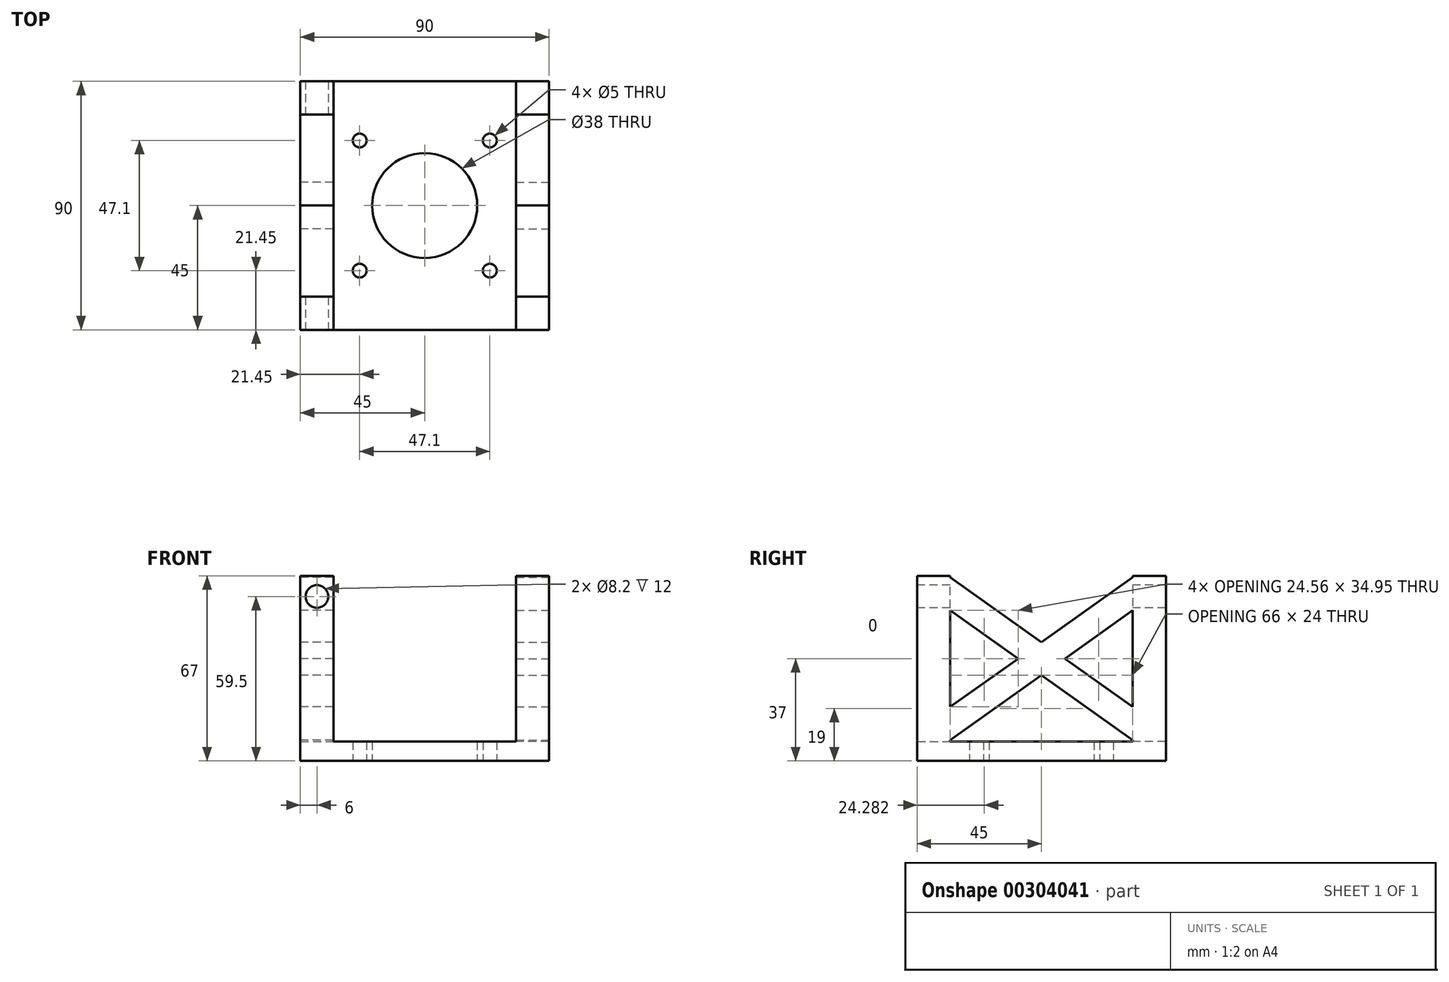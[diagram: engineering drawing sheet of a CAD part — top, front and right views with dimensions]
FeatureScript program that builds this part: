
annotation { "Feature Type Name" : "Feature", "Feature Type Description" : "" }
export const myFeature = defineFeature(function(context is Context, id is Id, definition is map)
    precondition{}
    {
        {
            var Q0;
            Q0=qCreatedBy(makeId("Top.planeOp"),FACE);
            var sketch = newSketch(context, id + "F0", { "sketchPlane" : qUnion([Q0])});
            skLineSegment(sketch, "E0.bottom", {"start": v(45, -45) * mm, "end": v(-45, -45) * mm});
            skLineSegment(sketch, "E0.top", {"start": v(45, 45) * mm, "end": v(-45, 45) * mm});
            skLineSegment(sketch, "E0.left", {"start": v(45, -45) * mm, "end": v(45, 45) * mm});
            skLineSegment(sketch, "E0.right", {"start": v(-45, -45) * mm, "end": v(-45, 45) * mm});
            skPoint(sketch, "E0.middle", {"position": v(0, 0) * mm});
            skLineSegment(sketch, "E1.bottom", {"start": v(23.55, -23.55) * mm, "end": v(-23.55, -23.55) * mm, "construction": true});
            skLineSegment(sketch, "E1.top", {"start": v(23.55, 23.55) * mm, "end": v(-23.55, 23.55) * mm, "construction": true});
            skLineSegment(sketch, "E1.left", {"start": v(23.55, -23.55) * mm, "end": v(23.55, 23.55) * mm, "construction": true});
            skLineSegment(sketch, "E1.right", {"start": v(-23.55, -23.55) * mm, "end": v(-23.55, 23.55) * mm, "construction": true});
            skCircle(sketch, "E2", {"center": v(0, 0) * mm, "radius": 19 * mm});
            skCircle(sketch, "E3", {"center": v(-23.55, 23.55) * mm, "radius": 2.5 * mm});
            skCircle(sketch, "E4", {"center": v(23.55, 23.55) * mm, "radius": 2.5 * mm});
            skCircle(sketch, "E5", {"center": v(23.55, -23.55) * mm, "radius": 2.5 * mm});
            skCircle(sketch, "E6", {"center": v(-23.55, -23.55) * mm, "radius": 2.5 * mm});
            skSolve(sketch);
        }
        {
            var Q0;
            Q0=makeQuery(id+"F0.imprint","IMPRINT",FACE,{"disambiguationData":[TD([[makeQuery(id+"F0.imprint","IMPRINT",EDGE,{"derivedFrom":sQuery(id+"F0.wireOp",EDGE,"E0.bottom")}),-1.0]])]});
            extrude(context, id + "F1", {"entities" : qUnion([Q0]), "depth" : 7 * mm});
        }
        {
            var Q0;
            Q0=makeQuery(id+"F1.opExtrude","CAP_FACE",FACE,{"disambiguationData":[OSD([sQuery(id+"F0.wireOp",EDGE,"E0.bottom"),sQuery(id+"F0.wireOp",EDGE,"E0.top"),sQuery(id+"F0.wireOp",EDGE,"E0.left"),sQuery(id+"F0.wireOp",EDGE,"E0.right")])],"isStart":false});
            cPlane(context, id + "F2", {"entities" : qUnion([Q0]), "cplaneType" : CPlaneType.OFFSET, "offset" : 0 * mm, "width" : 150 * mm, "height" : 150 * mm});
        }
        {
            var Q0;
            Q0=qCreatedBy(id+"F2.planeOp",FACE);
            var sketch = newSketch(context, id + "F3", { "sketchPlane" : qUnion([Q0])});
            skLineSegment(sketch, "E7.0.0", {"start": v(45, -45) * mm, "end": v(45, 45) * mm, "construction": true});
            skLineSegment(sketch, "E7.0.1", {"start": v(45, 45) * mm, "end": v(-45, 45) * mm, "construction": true});
            skLineSegment(sketch, "E7.0.2", {"start": v(-45, 45) * mm, "end": v(-45, -45) * mm, "construction": true});
            skLineSegment(sketch, "E7.0.3", {"start": v(-45, -45) * mm, "end": v(45, -45) * mm, "construction": true});
            skLineSegment(sketch, "E8.bottom", {"start": v(-45, 45) * mm, "end": v(-33, 45) * mm});
            skLineSegment(sketch, "E8.top", {"start": v(-45, 33) * mm, "end": v(-33, 33) * mm});
            skLineSegment(sketch, "E8.left", {"start": v(-45, 45) * mm, "end": v(-45, 33) * mm});
            skLineSegment(sketch, "E8.right", {"start": v(-33, 45) * mm, "end": v(-33, 33) * mm});
            skLineSegment(sketch, "E9.1.0", {"start": v(-45, -45) * mm, "end": v(-33, -45) * mm});
            skLineSegment(sketch, "E9.1.1", {"start": v(-45, -45) * mm, "end": v(-45, -33) * mm});
            skLineSegment(sketch, "E9.1.2", {"start": v(-33, -45) * mm, "end": v(-33, -33) * mm});
            skLineSegment(sketch, "E9.1.3", {"start": v(-45, -33) * mm, "end": v(-33, -33) * mm});
            skLineSegment(sketch, "E9.2.0", {"start": v(45, -45) * mm, "end": v(45, -33) * mm});
            skLineSegment(sketch, "E9.2.1", {"start": v(45, -45) * mm, "end": v(33, -45) * mm});
            skLineSegment(sketch, "E9.2.2", {"start": v(45, -33) * mm, "end": v(33, -33) * mm});
            skLineSegment(sketch, "E9.2.3", {"start": v(33, -45) * mm, "end": v(33, -33) * mm});
            skPoint(sketch, "E9.center", {"position": v(0, 0) * mm});
            skLineSegment(sketch, "E10.2.3.0", {"start": v(45, 45) * mm, "end": v(33, 45) * mm});
            skLineSegment(sketch, "E10.3.3.0", {"start": v(45, 45) * mm, "end": v(45, 33) * mm});
            skLineSegment(sketch, "E10.6.3.0", {"start": v(33, 45) * mm, "end": v(33, 33) * mm});
            skLineSegment(sketch, "E10.9.3.0", {"start": v(45, 33) * mm, "end": v(33, 33) * mm});
            skSolve(sketch);
        }
        {
            var Q0;
            Q0=makeQuery(id+"F3.imprint","IMPRINT",FACE,{"disambiguationData":[TD([[makeQuery(id+"F3.imprint","IMPRINT",EDGE,{"derivedFrom":sQuery(id+"F3.wireOp",EDGE,"E8.bottom")}),-1.0]])]});
            var Q1;
            Q1=makeQuery(id+"F3.imprint","IMPRINT",FACE,{"disambiguationData":[TD([[makeQuery(id+"F3.imprint","IMPRINT",EDGE,{"derivedFrom":sQuery(id+"F3.wireOp",EDGE,"E10.2.3.0")}),1.0]])]});
            var Q2;
            Q2=makeQuery(id+"F3.imprint","IMPRINT",FACE,{"disambiguationData":[TD([[makeQuery(id+"F3.imprint","IMPRINT",EDGE,{"derivedFrom":sQuery(id+"F3.wireOp",EDGE,"E9.2.0")}),1.0]])]});
            var Q3;
            Q3=makeQuery(id+"F3.imprint","IMPRINT",FACE,{"disambiguationData":[TD([[makeQuery(id+"F3.imprint","IMPRINT",EDGE,{"derivedFrom":sQuery(id+"F3.wireOp",EDGE,"E9.1.0")}),1.0]])]});
            extrude(context, id + "F4", {"entities" : qUnion([Q0, Q1, Q2, Q3]), "operationType" : NewBodyOperationType.ADD, "depth" : 60 * mm});
        }
        {
            var Q0;
            Q0=makeQuery(id+"F4.boolean.opBoolean","MERGE",FACE,{"derivedFrom":[makeQuery(id+"F1.opExtrude","SWEPT_FACE",FACE,{"disambiguationData":[OSD([sQuery(id+"F0.wireOp",EDGE,"E0.bottom")])]}),makeQuery(id+"F4.opExtrude","SWEPT_FACE",FACE,{"disambiguationData":[OSD([sQuery(id+"F3.wireOp",EDGE,"E9.1.0")])]}),makeQuery(id+"F4.opExtrude","SWEPT_FACE",FACE,{"disambiguationData":[OSD([sQuery(id+"F3.wireOp",EDGE,"E9.2.1")])]})]});
            cPlane(context, id + "F5", {"entities" : qUnion([Q0]), "cplaneType" : CPlaneType.OFFSET, "offset" : 0 * mm, "width" : 150 * mm, "height" : 150 * mm});
        }
        {
            var Q0;
            Q0=qCreatedBy(id+"F5.planeOp",FACE);
            var sketch = newSketch(context, id + "F6", { "sketchPlane" : qUnion([Q0])});
            skLineSegment(sketch, "E11.0", {"start": v(-45, 67) * mm, "end": v(-45, 0) * mm, "construction": true});
            skLineSegment(sketch, "E12.0", {"start": v(-45, 67) * mm, "end": v(-33, 67) * mm, "construction": true});
            skLineSegment(sketch, "E13", {"start": v(0, 0) * mm, "end": v(0, 101) * mm, "construction": true});
            skCircle(sketch, "E14", {"center": v(-39, 59.5) * mm, "radius": 4.1 * mm});
            skCircle(sketch, "E15.MirrorC", {"center": v(39, 59.5) * mm, "radius": 4.1 * mm});
            skSolve(sketch);
        }
        {
            var Q0;
            Q0=makeQuery(id+"F6.imprint","IMPRINT",FACE,{"disambiguationData":[TD([[makeQuery(id+"F6.imprint","IMPRINT",EDGE,{"derivedFrom":sQuery(id+"F6.wireOp",EDGE,"E14")}),1.0]])]});
            var Q1;
            Q1=makeQuery(id+"F6.imprint","IMPRINT",FACE,{"disambiguationData":[TD([[makeQuery(id+"F6.imprint","IMPRINT",EDGE,{"derivedFrom":sQuery(id+"F6.wireOp",EDGE,"E15.MirrorC")}),-1.0]])]});
            extrude(context, id + "F7", {"entities" : qUnion([Q0, Q1]), "operationType" : NewBodyOperationType.REMOVE, "oppositeDirection" : true, "depth" : 100 * mm});
        }
        {
            var Q0;
            Q0=makeQuery(id+"F0.imprint","IMPRINT",FACE,{"disambiguationData":[TD([[makeQuery(id+"F0.imprint","IMPRINT",EDGE,{"derivedFrom":sQuery(id+"F0.wireOp",EDGE,"E2")}),1.0]])]});
            var Q1;
            Q1=makeQuery(id+"F0.imprint","IMPRINT",FACE,{"disambiguationData":[TD([[makeQuery(id+"F0.imprint","IMPRINT",EDGE,{"derivedFrom":sQuery(id+"F0.wireOp",EDGE,"E3")}),1.0]])]});
            var Q2;
            Q2=makeQuery(id+"F0.imprint","IMPRINT",FACE,{"disambiguationData":[TD([[makeQuery(id+"F0.imprint","IMPRINT",EDGE,{"derivedFrom":sQuery(id+"F0.wireOp",EDGE,"E4")}),1.0]])]});
            var Q3;
            Q3=makeQuery(id+"F0.imprint","IMPRINT",FACE,{"disambiguationData":[TD([[makeQuery(id+"F0.imprint","IMPRINT",EDGE,{"derivedFrom":sQuery(id+"F0.wireOp",EDGE,"E5")}),1.0]])]});
            var Q4;
            Q4=makeQuery(id+"F0.imprint","IMPRINT",FACE,{"disambiguationData":[TD([[makeQuery(id+"F0.imprint","IMPRINT",EDGE,{"derivedFrom":sQuery(id+"F0.wireOp",EDGE,"E6")}),1.0]])]});
            extrude(context, id + "F8", {"entities" : qUnion([Q0, Q1, Q2, Q3, Q4]), "operationType" : NewBodyOperationType.REMOVE, "oppositeDirection" : true, "depth" : 25 * mm});
        }
        {
            var Q0;
            Q0=qCreatedBy(makeId("Top.planeOp"),FACE);
            var sketch = newSketch(context, id + "F9", { "sketchPlane" : qUnion([Q0])});
            skLineSegment(sketch, "E16.0", {"start": v(45, -45) * mm, "end": v(-45, -45) * mm});
            skLineSegment(sketch, "E17.0", {"start": v(-45, -45) * mm, "end": v(-45, 45) * mm});
            skLineSegment(sketch, "E18.0", {"start": v(45, -45) * mm, "end": v(45, 45) * mm});
            skLineSegment(sketch, "E19.0", {"start": v(45, 45) * mm, "end": v(-45, 45) * mm});
            skLineSegment(sketch, "E20.0", {"start": v(-33, -33) * mm, "end": v(-33, 29) * mm});
            skLineSegment(sketch, "E20.2", {"start": v(33, -33) * mm, "end": v(33, 29) * mm});
            skLineSegment(sketch, "E21", {"start": v(33, 29) * mm, "end": v(33, 45) * mm});
            skLineSegment(sketch, "E22", {"start": v(-33, 29) * mm, "end": v(-33, 45) * mm});
            skLineSegment(sketch, "E23", {"start": v(-33, -33) * mm, "end": v(-33, -45) * mm});
            skLineSegment(sketch, "E24", {"start": v(33, -33) * mm, "end": v(33, -45) * mm});
            skSolve(sketch);
        }
        {
            var Q0;
            Q0=makeQuery(id+"F4bZUCxmED6tgqa_1.boolean.opBoolean","MERGE",FACE,{"derivedFrom":[makeQuery(id+"F4.boolean.opBoolean","MERGE",FACE,{"derivedFrom":[makeQuery(id+"F1.opExtrude","SWEPT_FACE",FACE,{"disambiguationData":[OSD([sQuery(id+"F0.wireOp",EDGE,"E0.left")])]}),makeQuery(id+"F4.opExtrude","SWEPT_FACE",FACE,{"disambiguationData":[OSD([sQuery(id+"F3.wireOp",EDGE,"E9.2.0")])]}),makeQuery(id+"F4.opExtrude","SWEPT_FACE",FACE,{"disambiguationData":[OSD([sQuery(id+"F3.wireOp",EDGE,"E10.3.3.0")])]})]}),makeQuery(id+"F4bZUCxmED6tgqa_1.opExtrude","SWEPT_FACE",FACE,{"disambiguationData":[OSD([sQuery(id+"F9.wireOp",EDGE,"E18.0")])]})]});
            cPlane(context, id + "F10", {"entities" : qUnion([Q0]), "cplaneType" : CPlaneType.OFFSET, "offset" : 0 * mm, "width" : 150 * mm, "height" : 150 * mm});
        }
        {
            var Q0;
            Q0=qCreatedBy(id+"F10.planeOp",FACE);
            var sketch = newSketch(context, id + "F11", { "sketchPlane" : qUnion([Q0])});
            skLineSegment(sketch, "E25.0", {"start": v(0, 66.47) * mm, "end": v(0, 7) * mm, "construction": true});
            skLineSegment(sketch, "E26.0", {"start": v(-33, 37) * mm, "end": v(33, 37) * mm, "construction": true});
            skLineSegment(sketch, "E27", {"start": v(-33, 66.47) * mm, "end": v(-33, 54.47) * mm});
            skLineSegment(sketch, "E28.MirrorCS", {"start": v(-33, 7.53) * mm, "end": v(-33, 19.53) * mm});
            skLineSegment(sketch, "E29.MirrorCS", {"start": v(33, 66.47) * mm, "end": v(33, 54.47) * mm});
            skLineSegment(sketch, "E30.MirrorCS", {"start": v(33, 7.53) * mm, "end": v(33, 19.53) * mm});
            skLineSegment(sketch, "E31", {"start": v(-33, 54.47) * mm, "end": v(33, 7.53) * mm});
            skLineSegment(sketch, "E32", {"start": v(33, 66.47) * mm, "end": v(-33, 19.53) * mm});
            skLineSegment(sketch, "E33", {"start": v(33, 54.47) * mm, "end": v(-33, 7.53) * mm});
            skLineSegment(sketch, "E34", {"start": v(-33, 66.47) * mm, "end": v(33, 19.53) * mm});
            skSolve(sketch);
        }
        {
            var Q0;
            {var subQ0=sQuery(id+"F11.wireOp",EDGE,"E27");Q0=makeQuery(id+"F11.imprint","IMPRINT",FACE,{"disambiguationData":[TD([[makeQuery(id+"F11.imprint","IMPRINT",EDGE,{"derivedFrom":subQ0}),1.0]])]});}
            var Q1;
            {var subQ0=sQuery(id+"F11.wireOp",EDGE,"E29.MirrorCS");Q1=makeQuery(id+"F11.imprint","IMPRINT",FACE,{"disambiguationData":[TD([[makeQuery(id+"F11.imprint","IMPRINT",EDGE,{"derivedFrom":subQ0}),-1.0]])]});}
            var Q2;
            {var subQ0=sQuery(id+"F11.wireOp",EDGE,"E30.MirrorCS");Q2=makeQuery(id+"F11.imprint","IMPRINT",FACE,{"disambiguationData":[TD([[makeQuery(id+"F11.imprint","IMPRINT",EDGE,{"derivedFrom":subQ0}),1.0]])]});}
            var Q3;
            {var subQ0=sQuery(id+"F11.wireOp",EDGE,"E28.MirrorCS");Q3=makeQuery(id+"F11.imprint","IMPRINT",FACE,{"disambiguationData":[TD([[makeQuery(id+"F11.imprint","IMPRINT",EDGE,{"derivedFrom":subQ0}),-1.0]])]});}
            var Q4;
            {var subQ0=sQuery(id+"F11.wireOp",EDGE,"E32");var subQ1=sQuery(id+"F11.wireOp",EDGE,"E31");var subQ2=makeQuery(id+"F11.imprint","INTERSECT",VERTEX,{"derivedFrom":[subQ1,subQ0]});Q4=makeQuery(id+"F11.imprint","IMPRINT",FACE,{"disambiguationData":[TD([[makeQuery(id+"F11.imprint","IMPRINT",EDGE,{"disambiguationData":[TD([[subQ2,-1.0]])],"derivedFrom":subQ1}),1.0]])]});}
            extrude(context, id + "F12", {"entities" : qUnion([Q0, Q1, Q2, Q3, Q4]), "operationType" : NewBodyOperationType.ADD, "oppositeDirection" : true, "depth" : 12 * mm});
        }
        {
            var Q0;
            Q0=makeQuery(id+"F4.boolean.opBoolean","MERGE",FACE,{"derivedFrom":[makeQuery(id+"F1.opExtrude","SWEPT_FACE",FACE,{"disambiguationData":[OSD([sQuery(id+"F0.wireOp",EDGE,"E0.right")])]}),makeQuery(id+"F4.opExtrude","SWEPT_FACE",FACE,{"disambiguationData":[OSD([sQuery(id+"F3.wireOp",EDGE,"E8.left")])]}),makeQuery(id+"F4.opExtrude","SWEPT_FACE",FACE,{"disambiguationData":[OSD([sQuery(id+"F3.wireOp",EDGE,"E9.1.1")])]})]});
            cPlane(context, id + "F13", {"entities" : qUnion([Q0]), "cplaneType" : CPlaneType.OFFSET, "offset" : 0 * mm, "width" : 150 * mm, "height" : 150 * mm});
        }
        {
            var Q0;
            Q0=qCreatedBy(id+"F13.planeOp",FACE);
            var sketch = newSketch(context, id + "F14", { "sketchPlane" : qUnion([Q0])});
            skLineSegment(sketch, "E35.0", {"start": v(-33, 66.47) * mm, "end": v(0, 43) * mm});
            skLineSegment(sketch, "E36.0", {"start": v(33, 66.47) * mm, "end": v(0, 43) * mm});
            skLineSegment(sketch, "E37.0", {"start": v(33, 54.47) * mm, "end": v(8.44, 37) * mm});
            skLineSegment(sketch, "E38.0", {"start": v(8.44, 37) * mm, "end": v(33, 19.53) * mm});
            skLineSegment(sketch, "E39.0", {"start": v(0, 31) * mm, "end": v(33, 7.53) * mm});
            skLineSegment(sketch, "E40.0", {"start": v(0, 31) * mm, "end": v(-33, 7.53) * mm});
            skLineSegment(sketch, "E41.0", {"start": v(-8.44, 37) * mm, "end": v(-33, 19.53) * mm});
            skLineSegment(sketch, "E42.0", {"start": v(-33, 54.47) * mm, "end": v(-8.44, 37) * mm});
            skLineSegment(sketch, "E43.0", {"start": v(-33, 67) * mm, "end": v(-33, 7) * mm});
            skLineSegment(sketch, "E44.0", {"start": v(33, 67) * mm, "end": v(33, 7) * mm});
            skSolve(sketch);
        }
        {
            var Q0;
            {var subQ3=sQuery(id+"F14.wireOp",EDGE,"E35.0");Q0=makeQuery(id+"F14.imprint","IMPRINT",FACE,{"disambiguationData":[TD([[makeQuery(id+"F14.imprint","IMPRINT",EDGE,{"derivedFrom":subQ3}),-1.0]])]});}
            extrude(context, id + "F15", {"entities" : qUnion([Q0]), "operationType" : NewBodyOperationType.ADD, "oppositeDirection" : true, "depth" : 12 * mm});
        }
    });
